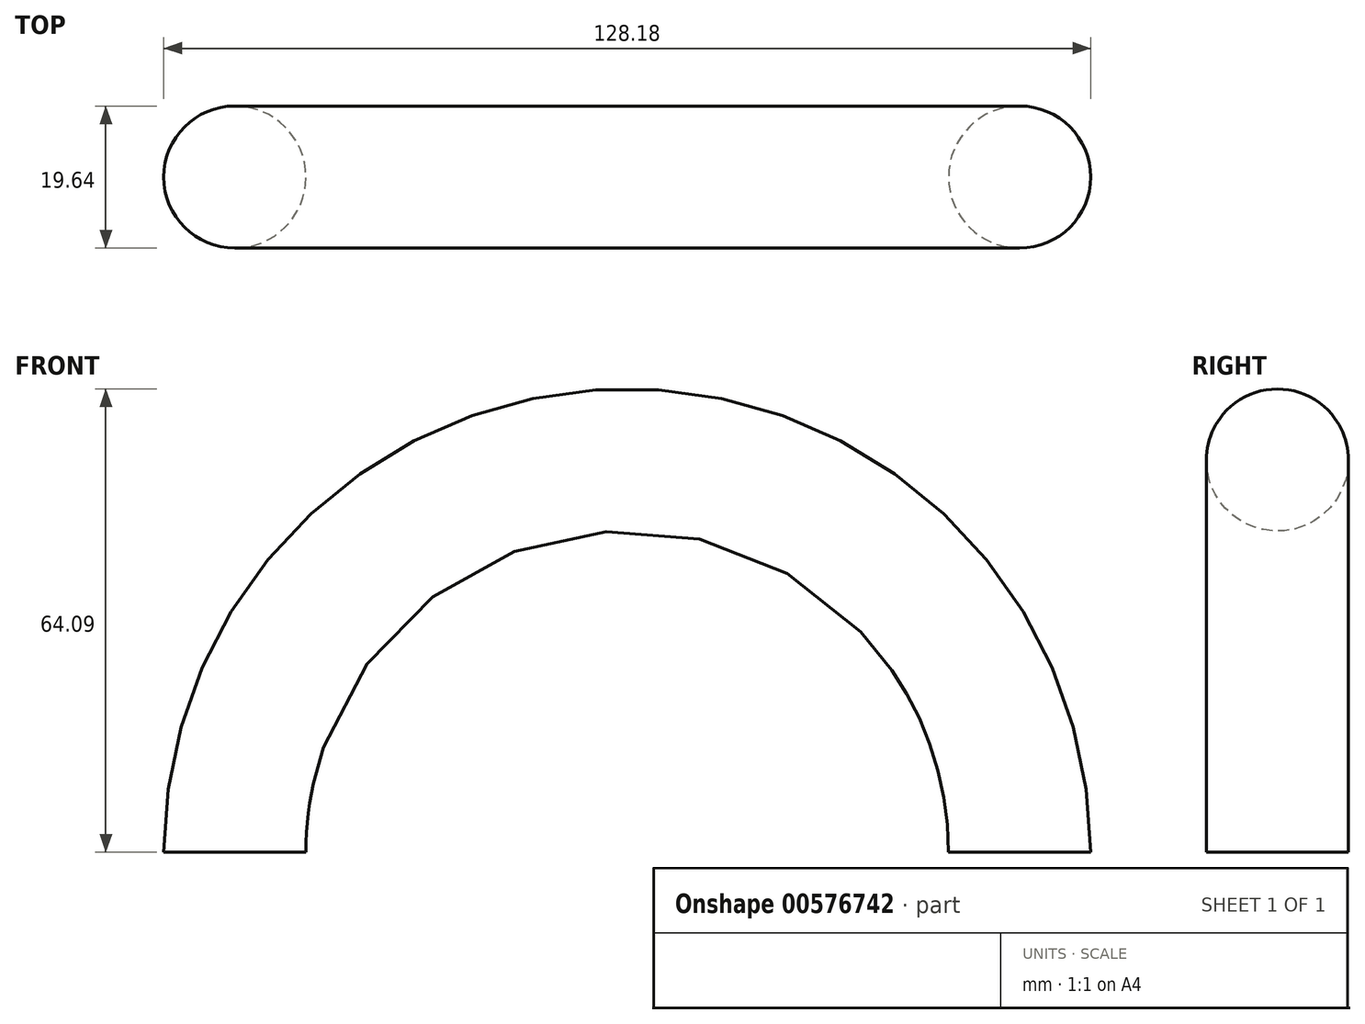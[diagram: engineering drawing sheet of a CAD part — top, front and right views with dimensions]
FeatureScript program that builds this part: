
annotation { "Feature Type Name" : "Feature", "Feature Type Description" : "" }
export const myFeature = defineFeature(function(context is Context, id is Id, definition is map)
    precondition{}
    {
        {
            var Q0;
            Q0=qCreatedBy(makeId("Top.planeOp"),FACE);
            var sketch = newSketch(context, id + "F0", { "sketchPlane" : qUnion([Q0])});
            skLineSegment(sketch, "E0.bottom", {"start": v(69.86, -68.76) * mm, "end": v(-69.86, -68.76) * mm});
            skLineSegment(sketch, "E0.top", {"start": v(69.86, 68.76) * mm, "end": v(-69.86, 68.76) * mm});
            skLineSegment(sketch, "E0.left", {"start": v(69.86, -68.76) * mm, "end": v(69.86, 68.76) * mm});
            skLineSegment(sketch, "E0.right", {"start": v(-69.86, -68.76) * mm, "end": v(-69.86, 68.76) * mm});
            skPoint(sketch, "E0.middle", {"position": v(0, 0) * mm});
            skLineSegment(sketch, "E1", {"start": v(0, 68.76) * mm, "end": v(0, -68.76) * mm});
            skSolve(sketch);
        }
        {
            var Q0;
            Q0=qCreatedBy(makeId("Top.planeOp"),FACE);
            var sketch = newSketch(context, id + "F1", { "sketchPlane" : qUnion([Q0])});
            skCircle(sketch, "E2", {"center": v(54.26, 0) * mm, "radius": 9.82 * mm});
            skSolve(sketch);
        }
        {
            var Q0;
            Q0=makeQuery(id+"F1.imprint","IMPRINT",FACE,{"disambiguationData":[TD([[makeQuery(id+"F1.imprint","IMPRINT",EDGE,{"derivedFrom":sQuery(id+"F1.wireOp",EDGE,"E2")}),1.0]])]});
            var Q1;
            Q1=sQuery(id+"F0.wireOp",EDGE,"E1");
            revolve(context, id + "F2", {"entities" : qUnion([Q0]), "axis" : qUnion([Q1]), "revolveType" : RevolveType.ONE_DIRECTION, "angle" : 180 * degree});
        }
    });
